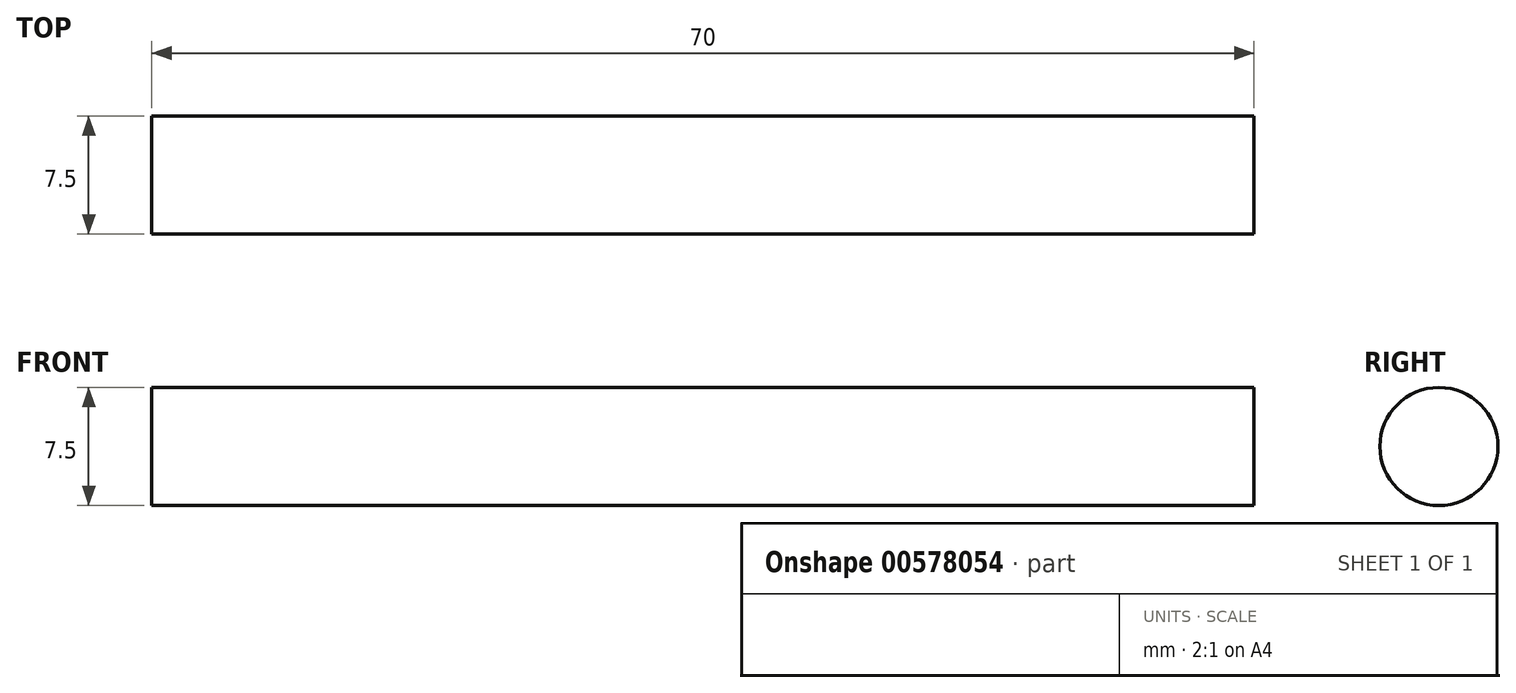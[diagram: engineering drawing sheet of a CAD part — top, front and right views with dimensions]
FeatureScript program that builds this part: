
annotation { "Feature Type Name" : "Feature", "Feature Type Description" : "" }
export const myFeature = defineFeature(function(context is Context, id is Id, definition is map)
    precondition{}
    {
        {
            var Q0;
            Q0=qCreatedBy(makeId("Right.planeOp"),FACE);
            var sketch = newSketch(context, id + "F0", { "sketchPlane" : qUnion([Q0])});
            skCircle(sketch, "E0", {"center": v(0, 0) * mm, "radius": 3.75 * mm});
            skSolve(sketch);
        }
        {
            var Q0;
            Q0 = qSketchRegion(id + "F0", true);
            extrude(context, id + "F1", {"entities" : qUnion([Q0]), "depth" : 70 * mm, "offsetDistance" : 25 * mm});
        }
    });
